# Revit family: Lavatory-Acorn-Dura_Ware-1953LC
name_source: partatom
category: Plumbing Fixtures
units: mm (PartAtom-declared; Revit-internal decimal feet)

## family parameters
Cut with Voids When Loaded = No
Host = Face
OmniClass Number = 23.45.05.14.14
OmniClass Title = Sinks/Lavatories
Part Type = Normal
Room Calculation Point = No
Round Connector Dimension = Use Diameter
Shared = Yes

## types (1)
- 1953LC-1-DMS-04-M
    -04-M Air-Control, Hot & Cold, Metering = Yes
    -1 Off-Floor, Wall Outlet = Yes
    -9 Without Valves with -H34 Punchingo (Must Specify Deck Punching) = No
    03-M - Air-Control, Single Temp, Metering = No
    ADA Compliant = Yes
    Assembly Code = D2010310
    BRS - Brass Body Valve = No
    CSG - Centerset with Gooseneck Spout and Wrist Blade Handles = No
    CW Connection = Yes
    CWFU = 1.5
    Cold Water Connection Diameter = 1/2"
    Cold Water Connection Radius = 1/4"
    Cold Water Connection Width = 4"
    DMS - Deck Mounted Spout = Yes
    Deck Punching Holes Diameter = 1 5/16"
    Deck Spout Material = Brass-Acorn-Chrome Plated
    Default Elevation = 0"
    Description = Front Mount, 20 inch x 22 inch ADA Compliant Stainless Steel Lavatory with Rectangle Bowl Configured for Mounting Carrier
    EE - Elbow Enclosure = No
    EG - Enviro-Glaze Color, Specify: = No
    Enclosure Visibility = No
    FG - 14 Gage Housing = No
    Flow Rate = if (DMS - Deck Mounted Spout) selected then 0.5 GPM
    GE-Grid Strainer w/ Close Elbow 1-1/4" = No
    GT-Grid Strainer w/ Tailpiece 1-1/4" = No
    H1 - Single Hole, On Center = No
    H24 - 4" Centered, Two Holes = No
    H28 - 8" Centerset, Two Holes = No
    H34 - 4" Centered, Three Holes = No
    H38 - 8" Centerset, Three Holes = No
    HW Connection = Yes
    HWFU = 1.5
    Height = 8"
    Hot Water Connection Diameter = 1/2"
    Hot Water Connection Radius = 1/4"
    Hot Water Connection Width = 4"
    IAPMO Compliance = Units to conform with ANSI, UFAS and ADA requirements for accessibility.
    Installation Type = Wall Mounted
    Length = 20"
    MVC1 - Time-Trol - Single Temp = No
    MVC2 - Time-Trol - Hot & Cold = No
    Manufacturer = Acorn
    Material = Stainless Steel-Acorn-Satin
    Model = 1953LC-1-DMS-04-M
    Mounting Height = 34"
    OF - Lavatory Overflow = No
    PPZ1 - Programmable Piezo Button - Single Temp w/9VDC Plug-In Transformer = No
    PPZ2 - Programmable Piezo Button - Hot & Cold w/9VDC Plug-In Transformer = No
    Product Documentation Link = https://www.acorneng.com
    Product Page URL = https://www.acorneng.com
    Sink Material = Stainless Steel-Acorn-Satin
    TE - Trap Enclosure = No
    TE Void Height = 1/16"
    TF - Transformer, 120VAC to 24VAC (-MVC option only) = No
    TPT-Tubular P-Trap 1-1/4" x 1-1/2" = No
    URL = https://www.acorneng.com
    Valve Cover B Dimension = 15 1/2"
    Valve Cover C Dimension = 7 3/4"
    Valve Cover D Dimension = 4"
    Valve Cover Depth = 4"
    Valve Cover Height A Dimension = 17 1/2"
    Valve Cover Height Constraint = 29"
    Valve Cover Length = 13 1/2"
    Valve Cover Plate Height = 29"
    Valve Cover Plate Height Constraint (General) = 29"
    Valve Cover Plate Height Constraint (TE) = 29"
    Valve Cover Visibility = Yes
    Vent Connection = No
    WFU = 2
    Wall Thickness /Type-Concrete/Block/Steel = No
    Waste Connection = Yes
    Waste Connection Diameter = 1 1/2"
    Width = 22"

## geometry (parser evidence)
native form markers: Sweep x2
no freeform markers — native parametric forms only
